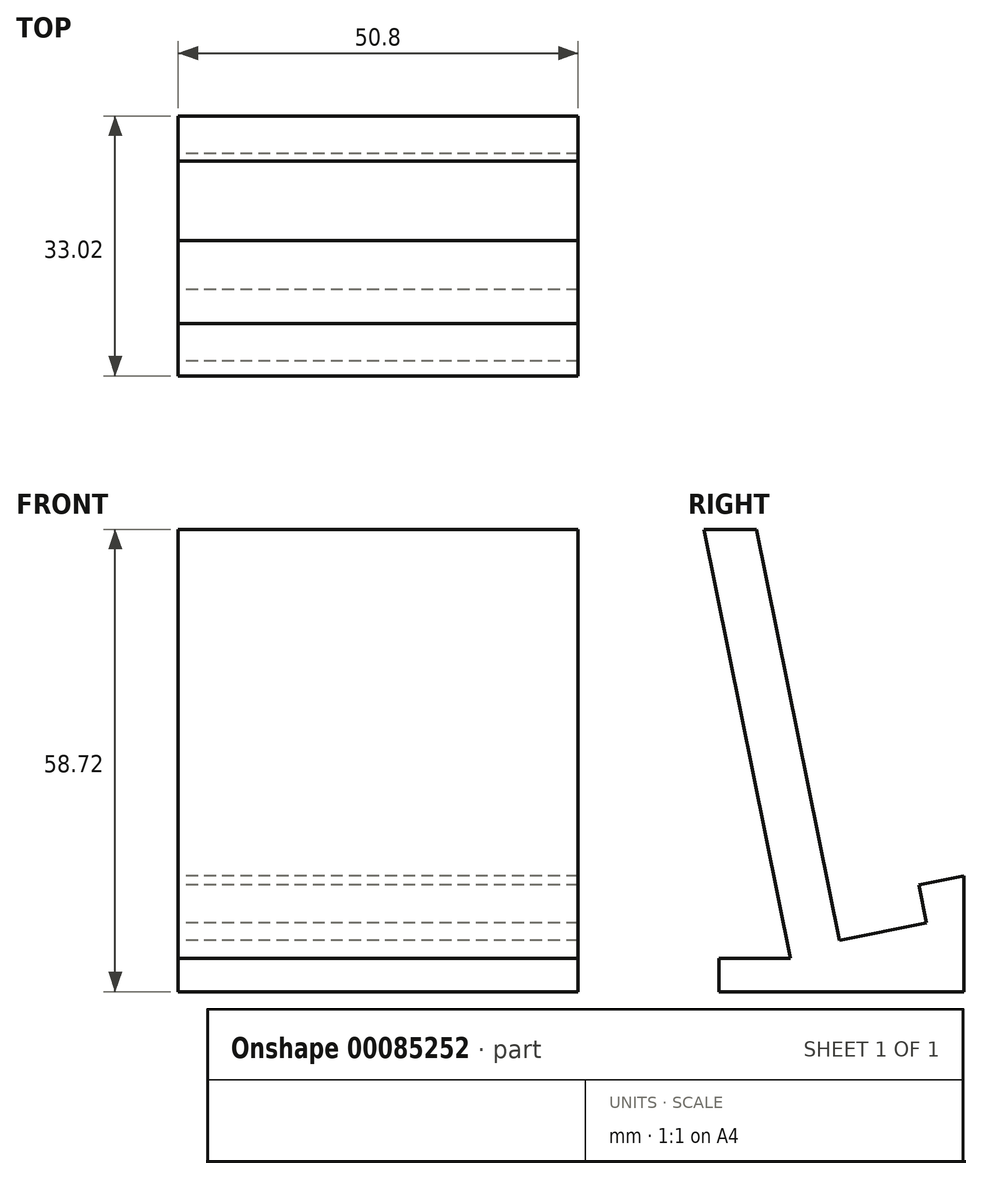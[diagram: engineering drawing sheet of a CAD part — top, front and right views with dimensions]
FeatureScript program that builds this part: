
annotation { "Feature Type Name" : "Feature", "Feature Type Description" : "" }
export const myFeature = defineFeature(function(context is Context, id is Id, definition is map)
    precondition{}
    {
        {
            var Q0;
            Q0=qCreatedBy(makeId("Right.planeOp"),FACE);
            var sketch = newSketch(context, id + "F0", { "sketchPlane" : qUnion([Q0])});
            skLineSegment(sketch, "E0", {"start": v(-11.56, 58.72) * mm, "end": v(-4.92, 58.72) * mm});
            skLineSegment(sketch, "E1", {"start": v(-4.92, 58.72) * mm, "end": v(5.6, 6.52) * mm});
            skLineSegment(sketch, "E2", {"start": v(5.6, 6.52) * mm, "end": v(16.7, 8.76) * mm});
            skLineSegment(sketch, "E3", {"start": v(16.7, 8.76) * mm, "end": v(15.73, 13.54) * mm});
            skLineSegment(sketch, "E4", {"start": v(15.73, 13.54) * mm, "end": v(21.46, 14.7) * mm});
            skLineSegment(sketch, "E5", {"start": v(21.46, 14.7) * mm, "end": v(21.46, 0) * mm});
            skLineSegment(sketch, "E6", {"start": v(21.46, 0) * mm, "end": v(4.92, 0) * mm});
            skLineSegment(sketch, "E7", {"start": v(-11.56, 58.72) * mm, "end": v(-0.57, 4.26) * mm});
            skLineSegment(sketch, "E8", {"start": v(-0.57, 4.26) * mm, "end": v(-9.65, 4.26) * mm});
            skLineSegment(sketch, "E9", {"start": v(-9.65, 4.26) * mm, "end": v(-9.65, 0) * mm});
            skLineSegment(sketch, "E10", {"start": v(-9.65, 0) * mm, "end": v(4.92, 0) * mm});
            skSolve(sketch);
        }
        {
            var Q0;
            Q0 = qSketchRegion(id + "F0", true);
            extrude(context, id + "F1", {"entities" : qUnion([Q0]), "depth" : 50.8 * mm});
        }
    });
